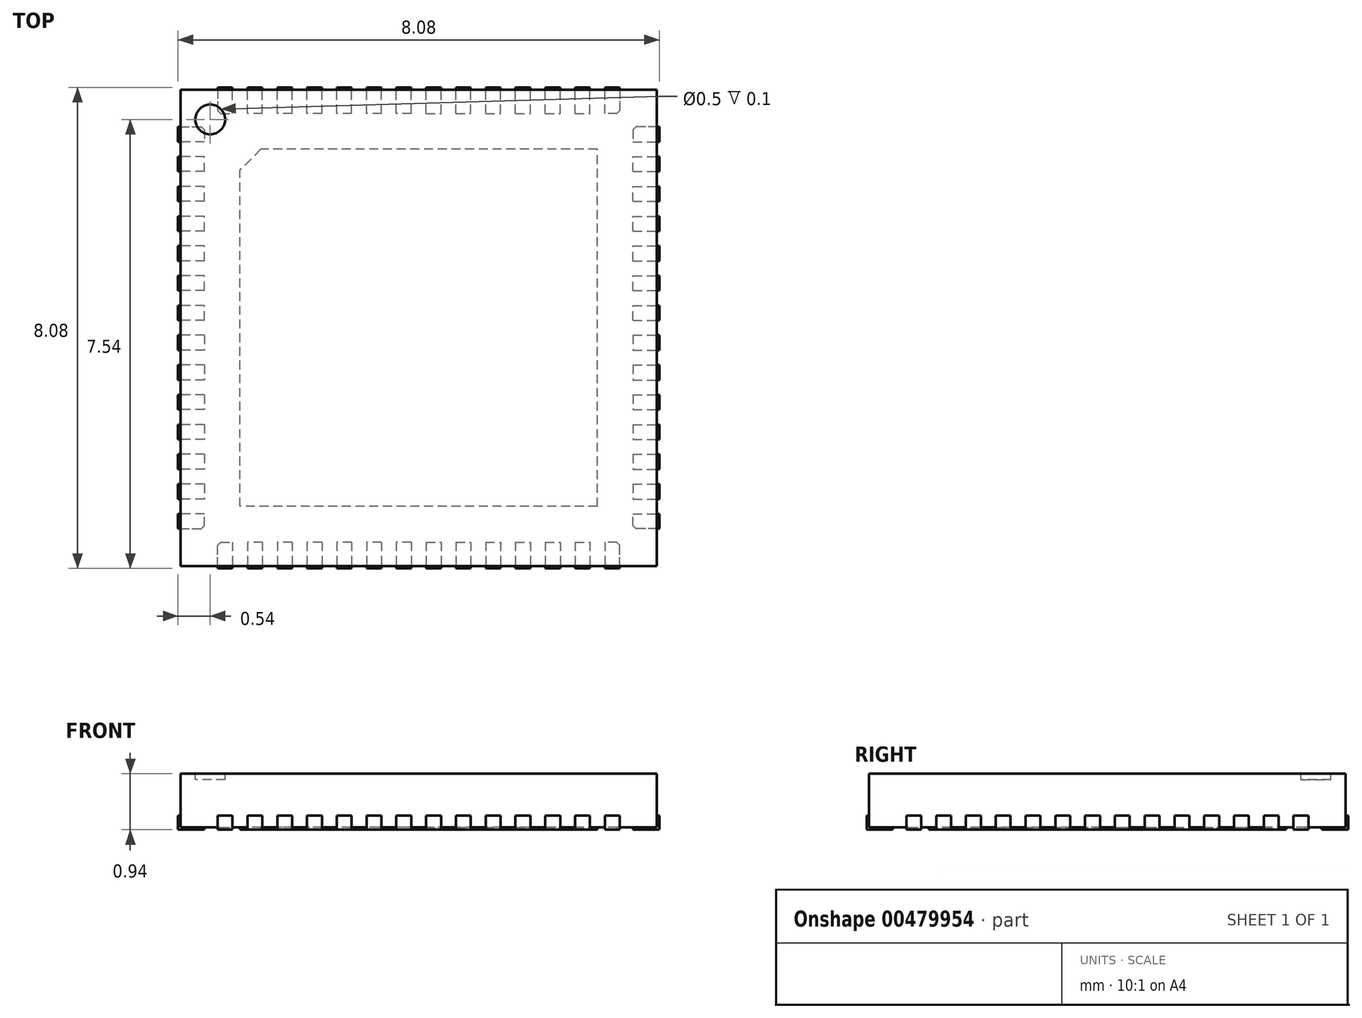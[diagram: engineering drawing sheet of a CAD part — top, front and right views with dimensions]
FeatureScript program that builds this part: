
annotation { "Feature Type Name" : "Feature", "Feature Type Description" : "" }
export const myFeature = defineFeature(function(context is Context, id is Id, definition is map)
    precondition{}
    {
        {
            var Q0;
            Q0=qCreatedBy(makeId("Top.planeOp"),FACE);
            var sketch = newSketch(context, id + "F0", { "sketchPlane" : qUnion([Q0])});
            skLineSegment(sketch, "E0.bottom", {"start": v(4, -4) * mm, "end": v(-4, -4) * mm});
            skLineSegment(sketch, "E0.top", {"start": v(4, 4) * mm, "end": v(-4, 4) * mm});
            skLineSegment(sketch, "E0.left", {"start": v(4, -4) * mm, "end": v(4, 4) * mm});
            skLineSegment(sketch, "E0.right", {"start": v(-4, -4) * mm, "end": v(-4, 4) * mm});
            skPoint(sketch, "E0.middle", {"position": v(0, 0) * mm});
            skSolve(sketch);
        }
        {
            var Q0;
            Q0 = qSketchRegion(id + "F0", true);
            extrude(context, id + "F1", {"entities" : qUnion([Q0]), "depth" : 0.9 * mm});
        }
        {
            var Q0;
            Q0=makeQuery(id+"F1.opExtrude","CAP_FACE",FACE,{"disambiguationData":[OSD([sQuery(id+"F0.wireOp",EDGE,"E0.bottom"),sQuery(id+"F0.wireOp",EDGE,"E0.top"),sQuery(id+"F0.wireOp",EDGE,"E0.left"),sQuery(id+"F0.wireOp",EDGE,"E0.right")])],"isStart":false});
            var sketch = newSketch(context, id + "F2", { "sketchPlane" : qUnion([Q0])});
            skCircle(sketch, "E1", {"center": v(-3.5, 3.5) * mm, "radius": 0.25 * mm});
            skSolve(sketch);
        }
        {
            var Q0;
            Q0 = qSketchRegion(id + "F2", true);
            extrude(context, id + "F3", {"entities" : qUnion([Q0]), "operationType" : NewBodyOperationType.REMOVE, "oppositeDirection" : true, "depth" : 0.1 * mm});
        }
        {
            var Q0;
            Q0=qCreatedBy(makeId("Top.planeOp"),FACE);
            cPlane(context, id + "F4", {"entities" : qUnion([Q0]), "cplaneType" : CPlaneType.OFFSET, "offset" : 0.2 * mm, "width" : 150 * mm, "height" : 150 * mm});
        }
        {
            var Q0;
            Q0=qCreatedBy(id+"F4.planeOp",FACE);
            var sketch = newSketch(context, id + "F5", { "sketchPlane" : qUnion([Q0])});
            skLineSegment(sketch, "E2.bottom", {"start": v(3.6, -2.63) * mm, "end": v(4.04, -2.63) * mm});
            skLineSegment(sketch, "E2.top", {"start": v(3.6, -2.88) * mm, "end": v(4.04, -2.88) * mm});
            skLineSegment(sketch, "E2.left", {"start": v(3.6, -2.63) * mm, "end": v(3.6, -2.88) * mm});
            skLineSegment(sketch, "E2.right", {"start": v(4.04, -2.63) * mm, "end": v(4.04, -2.88) * mm});
            skLineSegment(sketch, "E3.0.1.0", {"start": v(3.6, -2.13) * mm, "end": v(4.04, -2.13) * mm});
            skLineSegment(sketch, "E3.0.1.1", {"start": v(4.04, -2.13) * mm, "end": v(4.04, -2.38) * mm});
            skLineSegment(sketch, "E3.0.1.2", {"start": v(3.6, -2.13) * mm, "end": v(3.6, -2.38) * mm});
            skLineSegment(sketch, "E3.0.1.3", {"start": v(3.6, -2.38) * mm, "end": v(4.04, -2.38) * mm});
            skLineSegment(sketch, "E3.0.2.0", {"start": v(3.6, -1.63) * mm, "end": v(4.04, -1.63) * mm});
            skLineSegment(sketch, "E3.0.2.1", {"start": v(4.04, -1.63) * mm, "end": v(4.04, -1.88) * mm});
            skLineSegment(sketch, "E3.0.2.2", {"start": v(3.6, -1.63) * mm, "end": v(3.6, -1.88) * mm});
            skLineSegment(sketch, "E3.0.2.3", {"start": v(3.6, -1.88) * mm, "end": v(4.04, -1.88) * mm});
            skLineSegment(sketch, "E3.0.3.0", {"start": v(3.6, -1.13) * mm, "end": v(4.04, -1.13) * mm});
            skLineSegment(sketch, "E3.0.3.1", {"start": v(4.04, -1.13) * mm, "end": v(4.04, -1.38) * mm});
            skLineSegment(sketch, "E3.0.3.2", {"start": v(3.6, -1.13) * mm, "end": v(3.6, -1.38) * mm});
            skLineSegment(sketch, "E3.0.3.3", {"start": v(3.6, -1.38) * mm, "end": v(4.04, -1.38) * mm});
            skLineSegment(sketch, "E3.0.4.0", {"start": v(3.6, -0.63) * mm, "end": v(4.04, -0.63) * mm});
            skLineSegment(sketch, "E3.0.4.1", {"start": v(4.04, -0.63) * mm, "end": v(4.04, -0.88) * mm});
            skLineSegment(sketch, "E3.0.4.2", {"start": v(3.6, -0.63) * mm, "end": v(3.6, -0.88) * mm});
            skLineSegment(sketch, "E3.0.4.3", {"start": v(3.6, -0.88) * mm, "end": v(4.04, -0.88) * mm});
            skLineSegment(sketch, "E3.0.5.0", {"start": v(3.6, -0.13) * mm, "end": v(4.04, -0.13) * mm});
            skLineSegment(sketch, "E3.0.5.1", {"start": v(4.04, -0.12) * mm, "end": v(4.04, -0.37) * mm});
            skLineSegment(sketch, "E3.0.5.2", {"start": v(3.6, -0.13) * mm, "end": v(3.6, -0.37) * mm});
            skLineSegment(sketch, "E3.0.5.3", {"start": v(3.6, -0.37) * mm, "end": v(4.04, -0.37) * mm});
            skLineSegment(sketch, "E3.direction1", {"start": v(3.6, -2.88) * mm, "end": v(4.04, -2.88) * mm, "construction": true});
            skLineSegment(sketch, "E3.direction2", {"start": v(3.6, -2.88) * mm, "end": v(3.6, -2.38) * mm, "construction": true});
            skLineSegment(sketch, "E4", {"start": v(3.6, -3.13) * mm, "end": v(4.04, -3.13) * mm});
            skLineSegment(sketch, "E5", {"start": v(4.04, -3.13) * mm, "end": v(4.04, -3.38) * mm});
            skLineSegment(sketch, "E6", {"start": v(4.04, -3.38) * mm, "end": v(3.65, -3.38) * mm});
            skLineSegment(sketch, "E7", {"start": v(3.65, -3.38) * mm, "end": v(3.6, -3.33) * mm});
            skLineSegment(sketch, "E8", {"start": v(3.6, -3.33) * mm, "end": v(3.6, -3.13) * mm});
            skLineSegment(sketch, "E9", {"start": v(41.34, -41.34) * mm, "end": v(-33.82, 33.82) * mm, "construction": true});
            skLineSegment(sketch, "E10", {"start": v(54.18, 0) * mm, "end": v(-46.02, 0) * mm, "construction": true});
            skLineSegment(sketch, "E11.MirrorCS", {"start": v(3.38, -4.04) * mm, "end": v(3.38, -3.65) * mm});
            skLineSegment(sketch, "E12.MirrorCS", {"start": v(3.38, -3.65) * mm, "end": v(3.33, -3.6) * mm});
            skLineSegment(sketch, "E13.MirrorCS", {"start": v(3.13, -4.04) * mm, "end": v(3.38, -4.04) * mm});
            skLineSegment(sketch, "E14.MirrorCS", {"start": v(3.33, -3.6) * mm, "end": v(3.13, -3.6) * mm});
            skLineSegment(sketch, "E15.MirrorCS", {"start": v(3.13, -3.6) * mm, "end": v(3.13, -4.04) * mm});
            skLineSegment(sketch, "E16.MirrorCS", {"start": v(2.88, -3.6) * mm, "end": v(2.38, -3.6) * mm, "construction": true});
            skLineSegment(sketch, "E17.MirrorCS", {"start": v(0.13, -3.6) * mm, "end": v(0.37, -3.6) * mm});
            skLineSegment(sketch, "E18.MirrorCS", {"start": v(0.12, -4.04) * mm, "end": v(0.37, -4.04) * mm});
            skLineSegment(sketch, "E19.MirrorCS", {"start": v(1.63, -3.6) * mm, "end": v(1.88, -3.6) * mm});
            skLineSegment(sketch, "E20.MirrorCS", {"start": v(1.63, -4.04) * mm, "end": v(1.88, -4.04) * mm});
            skLineSegment(sketch, "E21.MirrorCS", {"start": v(2.13, -3.6) * mm, "end": v(2.38, -3.6) * mm});
            skLineSegment(sketch, "E22.MirrorCS", {"start": v(2.13, -4.04) * mm, "end": v(2.38, -4.04) * mm});
            skLineSegment(sketch, "E23.MirrorCS", {"start": v(2.63, -4.04) * mm, "end": v(2.88, -4.04) * mm});
            skLineSegment(sketch, "E24.MirrorCS", {"start": v(2.63, -3.6) * mm, "end": v(2.88, -3.6) * mm});
            skLineSegment(sketch, "E25.MirrorCS", {"start": v(1.13, -3.6) * mm, "end": v(1.38, -3.6) * mm});
            skLineSegment(sketch, "E26.MirrorCS", {"start": v(1.13, -4.04) * mm, "end": v(1.38, -4.04) * mm});
            skLineSegment(sketch, "E27.MirrorCS", {"start": v(1.88, -3.6) * mm, "end": v(1.88, -4.04) * mm});
            skLineSegment(sketch, "E28.MirrorCS", {"start": v(2.88, -3.6) * mm, "end": v(2.88, -4.04) * mm});
            skLineSegment(sketch, "E29.MirrorCS", {"start": v(0.63, -4.04) * mm, "end": v(0.88, -4.04) * mm});
            skLineSegment(sketch, "E30.MirrorCS", {"start": v(0.63, -3.6) * mm, "end": v(0.88, -3.6) * mm});
            skLineSegment(sketch, "E31.MirrorCS", {"start": v(0.88, -3.6) * mm, "end": v(0.88, -4.04) * mm});
            skLineSegment(sketch, "E32.MirrorCS", {"start": v(1.63, -3.6) * mm, "end": v(1.63, -4.04) * mm});
            skLineSegment(sketch, "E33.MirrorCS", {"start": v(2.38, -3.6) * mm, "end": v(2.38, -4.04) * mm});
            skLineSegment(sketch, "E34.MirrorCS", {"start": v(2.13, -3.6) * mm, "end": v(2.13, -4.04) * mm});
            skLineSegment(sketch, "E35.MirrorCS", {"start": v(2.88, -3.6) * mm, "end": v(2.88, -4.04) * mm, "construction": true});
            skLineSegment(sketch, "E36.MirrorCS", {"start": v(0.63, -3.6) * mm, "end": v(0.63, -4.04) * mm});
            skLineSegment(sketch, "E37.MirrorCS", {"start": v(0.38, -3.6) * mm, "end": v(0.38, -4.04) * mm});
            skLineSegment(sketch, "E38.MirrorCS", {"start": v(2.63, -3.6) * mm, "end": v(2.63, -4.04) * mm});
            skLineSegment(sketch, "E39.MirrorCS", {"start": v(1.38, -3.6) * mm, "end": v(1.38, -4.04) * mm});
            skLineSegment(sketch, "E40.MirrorCS", {"start": v(1.13, -3.6) * mm, "end": v(1.13, -4.04) * mm});
            skLineSegment(sketch, "E41.MirrorCS", {"start": v(0.13, -3.6) * mm, "end": v(0.13, -4.04) * mm});
            skLineSegment(sketch, "E42", {"start": v(0, -44.45) * mm, "end": v(0, 45.74) * mm, "construction": true});
            skLineSegment(sketch, "E43.MirrorCS", {"start": v(-3.33, -3.6) * mm, "end": v(-3.13, -3.6) * mm});
            skLineSegment(sketch, "E44.MirrorCS", {"start": v(-3.13, -4.04) * mm, "end": v(-3.38, -4.04) * mm});
            skLineSegment(sketch, "E45.MirrorCS", {"start": v(-3.38, -3.65) * mm, "end": v(-3.33, -3.6) * mm});
            skLineSegment(sketch, "E46.MirrorCS", {"start": v(-3.65, -3.38) * mm, "end": v(-3.6, -3.33) * mm});
            skLineSegment(sketch, "E47.MirrorCS", {"start": v(-4.04, -2.13) * mm, "end": v(-4.04, -2.38) * mm});
            skLineSegment(sketch, "E48.MirrorCS", {"start": v(-3.6, -2.13) * mm, "end": v(-3.6, -2.38) * mm});
            skLineSegment(sketch, "E49.MirrorCS", {"start": v(-4.04, -1.63) * mm, "end": v(-4.04, -1.88) * mm});
            skLineSegment(sketch, "E50.MirrorCS", {"start": v(-3.6, -1.63) * mm, "end": v(-3.6, -1.88) * mm});
            skLineSegment(sketch, "E51.MirrorCS", {"start": v(-0.63, -3.6) * mm, "end": v(-0.88, -3.6) * mm});
            skLineSegment(sketch, "E52.MirrorCS", {"start": v(-0.13, -3.6) * mm, "end": v(-0.37, -3.6) * mm});
            skLineSegment(sketch, "E53.MirrorCS", {"start": v(-3.6, -0.13) * mm, "end": v(-3.6, -0.37) * mm});
            skLineSegment(sketch, "E54.MirrorCS", {"start": v(-1.63, -3.6) * mm, "end": v(-1.88, -3.6) * mm});
            skLineSegment(sketch, "E55.MirrorCS", {"start": v(-0.12, -4.04) * mm, "end": v(-0.37, -4.04) * mm});
            skLineSegment(sketch, "E56.MirrorCS", {"start": v(-2.63, -4.04) * mm, "end": v(-2.88, -4.04) * mm});
            skLineSegment(sketch, "E57.MirrorCS", {"start": v(-3.6, -3.33) * mm, "end": v(-3.6, -3.13) * mm});
            skLineSegment(sketch, "E58.MirrorCS", {"start": v(-4.04, -2.63) * mm, "end": v(-4.04, -2.88) * mm});
            skLineSegment(sketch, "E59.MirrorCS", {"start": v(-3.6, -2.63) * mm, "end": v(-3.6, -2.88) * mm});
            skLineSegment(sketch, "E60.MirrorCS", {"start": v(-2.88, -3.6) * mm, "end": v(-2.38, -3.6) * mm, "construction": true});
            skLineSegment(sketch, "E61.MirrorCS", {"start": v(-3.6, -1.13) * mm, "end": v(-3.6, -1.38) * mm});
            skLineSegment(sketch, "E62.MirrorCS", {"start": v(-2.13, -4.04) * mm, "end": v(-2.38, -4.04) * mm});
            skLineSegment(sketch, "E63.MirrorCS", {"start": v(-1.13, -3.6) * mm, "end": v(-1.38, -3.6) * mm});
            skLineSegment(sketch, "E64.MirrorCS", {"start": v(-4.04, -0.12) * mm, "end": v(-4.04, -0.37) * mm});
            skLineSegment(sketch, "E65.MirrorCS", {"start": v(-0.63, -4.04) * mm, "end": v(-0.88, -4.04) * mm});
            skLineSegment(sketch, "E66.MirrorCS", {"start": v(-4.04, -3.13) * mm, "end": v(-4.04, -3.38) * mm});
            skLineSegment(sketch, "E67.MirrorCS", {"start": v(-1.63, -4.04) * mm, "end": v(-1.88, -4.04) * mm});
            skLineSegment(sketch, "E68.MirrorCS", {"start": v(-1.13, -4.04) * mm, "end": v(-1.38, -4.04) * mm});
            skLineSegment(sketch, "E69.MirrorCS", {"start": v(-4.04, -0.63) * mm, "end": v(-4.04, -0.88) * mm});
            skLineSegment(sketch, "E70.MirrorCS", {"start": v(-3.6, -2.88) * mm, "end": v(-3.6, -2.38) * mm, "construction": true});
            skLineSegment(sketch, "E71.MirrorCS", {"start": v(-2.13, -3.6) * mm, "end": v(-2.38, -3.6) * mm});
            skLineSegment(sketch, "E72.MirrorCS", {"start": v(-3.6, -0.63) * mm, "end": v(-3.6, -0.88) * mm});
            skLineSegment(sketch, "E73.MirrorCS", {"start": v(-2.63, -3.6) * mm, "end": v(-2.88, -3.6) * mm});
            skLineSegment(sketch, "E74.MirrorCS", {"start": v(-3.13, -3.6) * mm, "end": v(-3.13, -4.04) * mm});
            skLineSegment(sketch, "E75.MirrorCS", {"start": v(-4.04, -1.13) * mm, "end": v(-4.04, -1.38) * mm});
            skLineSegment(sketch, "E76.MirrorCS", {"start": v(-3.38, -4.04) * mm, "end": v(-3.38, -3.65) * mm});
            skLineSegment(sketch, "E77.MirrorCS", {"start": v(-4.04, -3.38) * mm, "end": v(-3.65, -3.38) * mm});
            skLineSegment(sketch, "E78.MirrorCS", {"start": v(-3.6, -1.88) * mm, "end": v(-4.04, -1.88) * mm});
            skLineSegment(sketch, "E79.MirrorCS", {"start": v(-3.6, -2.88) * mm, "end": v(-4.04, -2.88) * mm});
            skLineSegment(sketch, "E80.MirrorCS", {"start": v(-2.88, -3.6) * mm, "end": v(-2.88, -4.04) * mm});
            skLineSegment(sketch, "E81.MirrorCS", {"start": v(-3.6, -2.13) * mm, "end": v(-4.04, -2.13) * mm});
            skLineSegment(sketch, "E82.MirrorCS", {"start": v(-0.63, -3.6) * mm, "end": v(-0.63, -4.04) * mm});
            skLineSegment(sketch, "E83.MirrorCS", {"start": v(-3.6, -2.38) * mm, "end": v(-4.04, -2.38) * mm});
            skLineSegment(sketch, "E84.MirrorCS", {"start": v(-3.6, -1.63) * mm, "end": v(-4.04, -1.63) * mm});
            skLineSegment(sketch, "E85.MirrorCS", {"start": v(-41.34, -41.34) * mm, "end": v(33.82, 33.82) * mm, "construction": true});
            skLineSegment(sketch, "E86.MirrorCS", {"start": v(-3.6, -1.13) * mm, "end": v(-4.04, -1.13) * mm});
            skLineSegment(sketch, "E87.MirrorCS", {"start": v(-54.18, 0) * mm, "end": v(46.02, 0) * mm, "construction": true});
            skLineSegment(sketch, "E88.MirrorCS", {"start": v(-3.6, -0.63) * mm, "end": v(-4.04, -0.63) * mm});
            skLineSegment(sketch, "E89.MirrorCS", {"start": v(-3.6, -0.12) * mm, "end": v(-4.04, -0.12) * mm});
            skLineSegment(sketch, "E90.MirrorCS", {"start": v(-3.6, -2.63) * mm, "end": v(-4.04, -2.63) * mm});
            skLineSegment(sketch, "E91.MirrorCS", {"start": v(-3.6, -1.38) * mm, "end": v(-4.04, -1.38) * mm});
            skLineSegment(sketch, "E92.MirrorCS", {"start": v(-1.38, -3.6) * mm, "end": v(-1.38, -4.04) * mm});
            skLineSegment(sketch, "E93.MirrorCS", {"start": v(-3.6, -0.37) * mm, "end": v(-4.04, -0.37) * mm});
            skLineSegment(sketch, "E94.MirrorCS", {"start": v(-1.13, -3.6) * mm, "end": v(-1.13, -4.04) * mm});
            skLineSegment(sketch, "E95.MirrorCS", {"start": v(-3.6, -2.88) * mm, "end": v(-4.04, -2.88) * mm, "construction": true});
            skLineSegment(sketch, "E96.MirrorCS", {"start": v(-0.38, -3.6) * mm, "end": v(-0.38, -4.04) * mm});
            skLineSegment(sketch, "E97.MirrorCS", {"start": v(-0.88, -3.6) * mm, "end": v(-0.88, -4.04) * mm});
            skLineSegment(sketch, "E98.MirrorCS", {"start": v(-0.13, -3.6) * mm, "end": v(-0.13, -4.04) * mm});
            skLineSegment(sketch, "E99.MirrorCS", {"start": v(-1.88, -3.6) * mm, "end": v(-1.88, -4.04) * mm});
            skLineSegment(sketch, "E100.MirrorCS", {"start": v(-2.13, -3.6) * mm, "end": v(-2.13, -4.04) * mm});
            skLineSegment(sketch, "E101.MirrorCS", {"start": v(-2.88, -3.6) * mm, "end": v(-2.88, -4.04) * mm, "construction": true});
            skLineSegment(sketch, "E102.MirrorCS", {"start": v(-3.6, -0.88) * mm, "end": v(-4.04, -0.88) * mm});
            skLineSegment(sketch, "E103.MirrorCS", {"start": v(-1.63, -3.6) * mm, "end": v(-1.63, -4.04) * mm});
            skLineSegment(sketch, "E104.MirrorCS", {"start": v(-2.63, -3.6) * mm, "end": v(-2.63, -4.04) * mm});
            skLineSegment(sketch, "E105.MirrorCS", {"start": v(-2.38, -3.6) * mm, "end": v(-2.38, -4.04) * mm});
            skLineSegment(sketch, "E106.MirrorCS", {"start": v(-3.6, -3.13) * mm, "end": v(-4.04, -3.13) * mm});
            skLineSegment(sketch, "E107.MirrorCS", {"start": v(3.33, 3.6) * mm, "end": v(3.13, 3.6) * mm});
            skLineSegment(sketch, "E108.MirrorCS", {"start": v(3.38, 3.65) * mm, "end": v(3.33, 3.6) * mm});
            skLineSegment(sketch, "E109.MirrorCS", {"start": v(-3.13, 4.04) * mm, "end": v(-3.38, 4.04) * mm});
            skLineSegment(sketch, "E110.MirrorCS", {"start": v(-3.38, 3.65) * mm, "end": v(-3.33, 3.6) * mm});
            skLineSegment(sketch, "E111.MirrorCS", {"start": v(3.13, 4.04) * mm, "end": v(3.38, 4.04) * mm});
            skLineSegment(sketch, "E112.MirrorCS", {"start": v(-3.33, 3.6) * mm, "end": v(-3.13, 3.6) * mm});
            skLineSegment(sketch, "E113.MirrorCS", {"start": v(3.65, 3.38) * mm, "end": v(3.6, 3.33) * mm});
            skLineSegment(sketch, "E114.MirrorCS", {"start": v(-3.6, 0.12) * mm, "end": v(-3.6, 0.37) * mm});
            skLineSegment(sketch, "E115.MirrorCS", {"start": v(4.04, 3.13) * mm, "end": v(4.04, 3.38) * mm});
            skLineSegment(sketch, "E116.MirrorCS", {"start": v(2.88, 3.6) * mm, "end": v(2.38, 3.6) * mm, "construction": true});
            skLineSegment(sketch, "E117.MirrorCS", {"start": v(0.63, 4.04) * mm, "end": v(0.88, 4.04) * mm});
            skLineSegment(sketch, "E118.MirrorCS", {"start": v(-4.04, 0.62) * mm, "end": v(-4.04, 0.87) * mm});
            skLineSegment(sketch, "E119.MirrorCS", {"start": v(-4.04, 2.13) * mm, "end": v(-4.04, 2.38) * mm});
            skLineSegment(sketch, "E120.MirrorCS", {"start": v(-4.04, 1.13) * mm, "end": v(-4.04, 1.38) * mm});
            skLineSegment(sketch, "E121.MirrorCS", {"start": v(1.63, 4.04) * mm, "end": v(1.88, 4.04) * mm});
            skLineSegment(sketch, "E122.MirrorCS", {"start": v(-0.13, 3.6) * mm, "end": v(-0.37, 3.6) * mm});
            skLineSegment(sketch, "E123.MirrorCS", {"start": v(-1.13, 4.04) * mm, "end": v(-1.38, 4.04) * mm});
            skLineSegment(sketch, "E124.MirrorCS", {"start": v(-3.6, 2.63) * mm, "end": v(-3.6, 2.88) * mm});
            skLineSegment(sketch, "E125.MirrorCS", {"start": v(-0.63, 3.6) * mm, "end": v(-0.88, 3.6) * mm});
            skLineSegment(sketch, "E126.MirrorCS", {"start": v(-1.63, 4.04) * mm, "end": v(-1.88, 4.04) * mm});
            skLineSegment(sketch, "E127.MirrorCS", {"start": v(3.6, 2.88) * mm, "end": v(3.6, 2.38) * mm, "construction": true});
            skLineSegment(sketch, "E128.MirrorCS", {"start": v(-3.6, 1.63) * mm, "end": v(-3.6, 1.88) * mm});
            skLineSegment(sketch, "E129.MirrorCS", {"start": v(1.13, 4.04) * mm, "end": v(1.38, 4.04) * mm});
            skLineSegment(sketch, "E130.MirrorCS", {"start": v(-3.65, 3.38) * mm, "end": v(-3.6, 3.33) * mm});
            skLineSegment(sketch, "E131.MirrorCS", {"start": v(-1.13, 3.6) * mm, "end": v(-1.38, 3.6) * mm});
            skLineSegment(sketch, "E132.MirrorCS", {"start": v(-0.63, 4.04) * mm, "end": v(-0.88, 4.04) * mm});
            skLineSegment(sketch, "E133.MirrorCS", {"start": v(2.13, 3.6) * mm, "end": v(2.38, 3.6) * mm});
            skLineSegment(sketch, "E134.MirrorCS", {"start": v(-4.04, 3.13) * mm, "end": v(-4.04, 3.38) * mm});
            skLineSegment(sketch, "E135.MirrorCS", {"start": v(-2.63, 3.6) * mm, "end": v(-2.88, 3.6) * mm});
            skLineSegment(sketch, "E136.MirrorCS", {"start": v(-3.6, 0.62) * mm, "end": v(-3.6, 0.87) * mm});
            skLineSegment(sketch, "E137.MirrorCS", {"start": v(-2.88, 3.6) * mm, "end": v(-2.38, 3.6) * mm, "construction": true});
            skLineSegment(sketch, "E138.MirrorCS", {"start": v(-2.63, 4.04) * mm, "end": v(-2.88, 4.04) * mm});
            skLineSegment(sketch, "E139.MirrorCS", {"start": v(3.6, 3.33) * mm, "end": v(3.6, 3.13) * mm});
            skLineSegment(sketch, "E140.MirrorCS", {"start": v(-1.63, 3.6) * mm, "end": v(-1.88, 3.6) * mm});
            skLineSegment(sketch, "E141.MirrorCS", {"start": v(-3.6, 2.88) * mm, "end": v(-3.6, 2.38) * mm, "construction": true});
            skLineSegment(sketch, "E142.MirrorCS", {"start": v(0.13, 3.6) * mm, "end": v(0.37, 3.6) * mm});
            skLineSegment(sketch, "E143.MirrorCS", {"start": v(-3.13, 3.6) * mm, "end": v(-3.13, 4.04) * mm});
            skLineSegment(sketch, "E144.MirrorCS", {"start": v(3.6, 0.62) * mm, "end": v(3.6, 0.87) * mm});
            skLineSegment(sketch, "E145.MirrorCS", {"start": v(3.38, 4.04) * mm, "end": v(3.38, 3.65) * mm});
            skLineSegment(sketch, "E146.MirrorCS", {"start": v(1.63, 3.6) * mm, "end": v(1.88, 3.6) * mm});
            skLineSegment(sketch, "E147.MirrorCS", {"start": v(-3.6, 3.33) * mm, "end": v(-3.6, 3.13) * mm});
            skLineSegment(sketch, "E148.MirrorCS", {"start": v(-0.12, 4.04) * mm, "end": v(-0.37, 4.04) * mm});
            skLineSegment(sketch, "E149.MirrorCS", {"start": v(0.12, 4.04) * mm, "end": v(0.37, 4.04) * mm});
            skLineSegment(sketch, "E150.MirrorCS", {"start": v(-4.04, 2.63) * mm, "end": v(-4.04, 2.88) * mm});
            skLineSegment(sketch, "E151.MirrorCS", {"start": v(-2.13, 3.6) * mm, "end": v(-2.38, 3.6) * mm});
            skLineSegment(sketch, "E152.MirrorCS", {"start": v(2.13, 4.04) * mm, "end": v(2.38, 4.04) * mm});
            skLineSegment(sketch, "E153.MirrorCS", {"start": v(4.04, 0.12) * mm, "end": v(4.04, 0.37) * mm});
            skLineSegment(sketch, "E154.MirrorCS", {"start": v(-4.04, 0.12) * mm, "end": v(-4.04, 0.37) * mm});
            skLineSegment(sketch, "E155.MirrorCS", {"start": v(-3.6, 2.13) * mm, "end": v(-3.6, 2.38) * mm});
            skLineSegment(sketch, "E156.MirrorCS", {"start": v(0.63, 3.6) * mm, "end": v(0.88, 3.6) * mm});
            skLineSegment(sketch, "E157.MirrorCS", {"start": v(-2.13, 4.04) * mm, "end": v(-2.38, 4.04) * mm});
            skLineSegment(sketch, "E158.MirrorCS", {"start": v(3.6, 0.12) * mm, "end": v(3.6, 0.37) * mm});
            skLineSegment(sketch, "E159.MirrorCS", {"start": v(-3.6, 1.13) * mm, "end": v(-3.6, 1.38) * mm});
            skLineSegment(sketch, "E160.MirrorCS", {"start": v(2.63, 3.6) * mm, "end": v(2.88, 3.6) * mm});
            skLineSegment(sketch, "E161.MirrorCS", {"start": v(3.13, 3.6) * mm, "end": v(3.13, 4.04) * mm});
            skLineSegment(sketch, "E162.MirrorCS", {"start": v(4.04, 1.63) * mm, "end": v(4.04, 1.88) * mm});
            skLineSegment(sketch, "E163.MirrorCS", {"start": v(3.6, 2.13) * mm, "end": v(3.6, 2.38) * mm});
            skLineSegment(sketch, "E164.MirrorCS", {"start": v(4.04, 2.13) * mm, "end": v(4.04, 2.38) * mm});
            skLineSegment(sketch, "E165.MirrorCS", {"start": v(3.6, 1.63) * mm, "end": v(3.6, 1.88) * mm});
            skLineSegment(sketch, "E166.MirrorCS", {"start": v(1.13, 3.6) * mm, "end": v(1.38, 3.6) * mm});
            skLineSegment(sketch, "E167.MirrorCS", {"start": v(2.63, 4.04) * mm, "end": v(2.88, 4.04) * mm});
            skLineSegment(sketch, "E168.MirrorCS", {"start": v(3.6, 1.13) * mm, "end": v(3.6, 1.38) * mm});
            skLineSegment(sketch, "E169.MirrorCS", {"start": v(-3.38, 4.04) * mm, "end": v(-3.38, 3.65) * mm});
            skLineSegment(sketch, "E170.MirrorCS", {"start": v(4.04, 1.13) * mm, "end": v(4.04, 1.38) * mm});
            skLineSegment(sketch, "E171.MirrorCS", {"start": v(-4.04, 1.63) * mm, "end": v(-4.04, 1.88) * mm});
            skLineSegment(sketch, "E172.MirrorCS", {"start": v(4.04, 2.63) * mm, "end": v(4.04, 2.88) * mm});
            skLineSegment(sketch, "E173.MirrorCS", {"start": v(4.04, 0.62) * mm, "end": v(4.04, 0.87) * mm});
            skLineSegment(sketch, "E174.MirrorCS", {"start": v(3.6, 2.63) * mm, "end": v(3.6, 2.88) * mm});
            skLineSegment(sketch, "E175.MirrorCS", {"start": v(-2.88, 3.6) * mm, "end": v(-2.88, 4.04) * mm});
            skLineSegment(sketch, "E176.MirrorCS", {"start": v(3.6, 1.88) * mm, "end": v(4.04, 1.88) * mm});
            skLineSegment(sketch, "E177.MirrorCS", {"start": v(4.04, 3.38) * mm, "end": v(3.65, 3.38) * mm});
            skLineSegment(sketch, "E178.MirrorCS", {"start": v(2.88, 3.6) * mm, "end": v(2.88, 4.04) * mm});
            skLineSegment(sketch, "E179.MirrorCS", {"start": v(-3.6, 2.88) * mm, "end": v(-4.04, 2.88) * mm});
            skLineSegment(sketch, "E180.MirrorCS", {"start": v(3.6, 2.88) * mm, "end": v(4.04, 2.88) * mm});
            skLineSegment(sketch, "E181.MirrorCS", {"start": v(-3.6, 2.38) * mm, "end": v(-4.04, 2.38) * mm});
            skLineSegment(sketch, "E182.MirrorCS", {"start": v(-0.88, 3.6) * mm, "end": v(-0.88, 4.04) * mm});
            skLineSegment(sketch, "E183.MirrorCS", {"start": v(-1.63, 3.6) * mm, "end": v(-1.63, 4.04) * mm});
            skLineSegment(sketch, "E184.MirrorCS", {"start": v(2.38, 3.6) * mm, "end": v(2.38, 4.04) * mm});
            skLineSegment(sketch, "E185.MirrorCS", {"start": v(-0.63, 3.6) * mm, "end": v(-0.63, 4.04) * mm});
            skLineSegment(sketch, "E186.MirrorCS", {"start": v(-0.38, 3.6) * mm, "end": v(-0.38, 4.04) * mm});
            skLineSegment(sketch, "E187.MirrorCS", {"start": v(-3.6, 2.13) * mm, "end": v(-4.04, 2.13) * mm});
            skLineSegment(sketch, "E188.MirrorCS", {"start": v(1.13, 3.6) * mm, "end": v(1.13, 4.04) * mm});
            skLineSegment(sketch, "E189.MirrorCS", {"start": v(-4.04, 3.38) * mm, "end": v(-3.65, 3.38) * mm});
            skLineSegment(sketch, "E190.MirrorCS", {"start": v(-3.6, 3.13) * mm, "end": v(-4.04, 3.13) * mm});
            skLineSegment(sketch, "E191.MirrorCS", {"start": v(3.6, 0.12) * mm, "end": v(4.04, 0.12) * mm});
            skLineSegment(sketch, "E192.MirrorCS", {"start": v(-1.13, 3.6) * mm, "end": v(-1.13, 4.04) * mm});
            skLineSegment(sketch, "E193.MirrorCS", {"start": v(3.6, 0.37) * mm, "end": v(4.04, 0.37) * mm});
            skLineSegment(sketch, "E194.MirrorCS", {"start": v(-3.6, 2.88) * mm, "end": v(-4.04, 2.88) * mm, "construction": true});
            skLineSegment(sketch, "E195.MirrorCS", {"start": v(0.38, 3.6) * mm, "end": v(0.38, 4.04) * mm});
            skLineSegment(sketch, "E196.MirrorCS", {"start": v(-3.6, 1.13) * mm, "end": v(-4.04, 1.13) * mm});
            skLineSegment(sketch, "E197.MirrorCS", {"start": v(-2.13, 3.6) * mm, "end": v(-2.13, 4.04) * mm});
            skLineSegment(sketch, "E198.MirrorCS", {"start": v(2.13, 3.6) * mm, "end": v(2.13, 4.04) * mm});
            skLineSegment(sketch, "E199.MirrorCS", {"start": v(0.88, 3.6) * mm, "end": v(0.88, 4.04) * mm});
            skLineSegment(sketch, "E200.MirrorCS", {"start": v(3.6, 1.13) * mm, "end": v(4.04, 1.13) * mm});
            skLineSegment(sketch, "E201.MirrorCS", {"start": v(-3.6, 1.63) * mm, "end": v(-4.04, 1.63) * mm});
            skLineSegment(sketch, "E202.MirrorCS", {"start": v(-0.13, 3.6) * mm, "end": v(-0.13, 4.04) * mm});
            skLineSegment(sketch, "E203.MirrorCS", {"start": v(-2.88, 3.6) * mm, "end": v(-2.88, 4.04) * mm, "construction": true});
            skLineSegment(sketch, "E204.MirrorCS", {"start": v(-3.6, 1.88) * mm, "end": v(-4.04, 1.88) * mm});
            skLineSegment(sketch, "E205.MirrorCS", {"start": v(-1.38, 3.6) * mm, "end": v(-1.38, 4.04) * mm});
            skLineSegment(sketch, "E206.MirrorCS", {"start": v(3.6, 3.13) * mm, "end": v(4.04, 3.13) * mm});
            skLineSegment(sketch, "E207.MirrorCS", {"start": v(-3.6, 0.62) * mm, "end": v(-4.04, 0.62) * mm});
            skLineSegment(sketch, "E208.MirrorCS", {"start": v(-3.6, 0.87) * mm, "end": v(-4.04, 0.87) * mm});
            skLineSegment(sketch, "E209.MirrorCS", {"start": v(1.63, 3.6) * mm, "end": v(1.63, 4.04) * mm});
            skLineSegment(sketch, "E210.MirrorCS", {"start": v(3.6, 2.88) * mm, "end": v(4.04, 2.88) * mm, "construction": true});
            skLineSegment(sketch, "E211.MirrorCS", {"start": v(-1.88, 3.6) * mm, "end": v(-1.88, 4.04) * mm});
            skLineSegment(sketch, "E212.MirrorCS", {"start": v(-3.6, 2.63) * mm, "end": v(-4.04, 2.63) * mm});
            skLineSegment(sketch, "E213.MirrorCS", {"start": v(3.6, 0.62) * mm, "end": v(4.04, 0.62) * mm});
            skLineSegment(sketch, "E214.MirrorCS", {"start": v(-2.38, 3.6) * mm, "end": v(-2.38, 4.04) * mm});
            skLineSegment(sketch, "E215.MirrorCS", {"start": v(2.88, 3.6) * mm, "end": v(2.88, 4.04) * mm, "construction": true});
            skLineSegment(sketch, "E216.MirrorCS", {"start": v(-3.6, 1.38) * mm, "end": v(-4.04, 1.38) * mm});
            skLineSegment(sketch, "E217.MirrorCS", {"start": v(3.6, 0.87) * mm, "end": v(4.04, 0.87) * mm});
            skLineSegment(sketch, "E218.MirrorCS", {"start": v(2.63, 3.6) * mm, "end": v(2.63, 4.04) * mm});
            skLineSegment(sketch, "E219.MirrorCS", {"start": v(3.6, 1.38) * mm, "end": v(4.04, 1.38) * mm});
            skLineSegment(sketch, "E220.MirrorCS", {"start": v(0.63, 3.6) * mm, "end": v(0.63, 4.04) * mm});
            skLineSegment(sketch, "E221.MirrorCS", {"start": v(3.6, 2.63) * mm, "end": v(4.04, 2.63) * mm});
            skLineSegment(sketch, "E222.MirrorCS", {"start": v(3.6, 1.63) * mm, "end": v(4.04, 1.63) * mm});
            skLineSegment(sketch, "E223.MirrorCS", {"start": v(3.6, 2.38) * mm, "end": v(4.04, 2.38) * mm});
            skLineSegment(sketch, "E224.MirrorCS", {"start": v(1.38, 3.6) * mm, "end": v(1.38, 4.04) * mm});
            skLineSegment(sketch, "E225.MirrorCS", {"start": v(-3.6, 0.12) * mm, "end": v(-4.04, 0.12) * mm});
            skLineSegment(sketch, "E226.MirrorCS", {"start": v(3.6, 2.13) * mm, "end": v(4.04, 2.13) * mm});
            skLineSegment(sketch, "E227.MirrorCS", {"start": v(-3.6, 0.37) * mm, "end": v(-4.04, 0.37) * mm});
            skLineSegment(sketch, "E228.MirrorCS", {"start": v(1.88, 3.6) * mm, "end": v(1.88, 4.04) * mm});
            skLineSegment(sketch, "E229.MirrorCS", {"start": v(-2.63, 3.6) * mm, "end": v(-2.63, 4.04) * mm});
            skLineSegment(sketch, "E230.MirrorCS", {"start": v(0.13, 3.6) * mm, "end": v(0.13, 4.04) * mm});
            skPoint(sketch, "E231.middle", {"position": v(0, 0) * mm});
            skSolve(sketch);
        }
        {
            var Q0;
            Q0=qCreatedBy(id+"F4.planeOp",FACE);
            var sketch = newSketch(context, id + "F6", { "sketchPlane" : qUnion([Q0])});
            skLineSegment(sketch, "E232.bottom", {"start": v(3.6, 3.6) * mm, "end": v(-3.6, 3.6) * mm});
            skLineSegment(sketch, "E232.top", {"start": v(3.6, -3.6) * mm, "end": v(-3.6, -3.6) * mm});
            skLineSegment(sketch, "E232.left", {"start": v(3.6, 3.6) * mm, "end": v(3.6, -3.6) * mm});
            skLineSegment(sketch, "E232.right", {"start": v(-3.6, 3.6) * mm, "end": v(-3.6, -3.6) * mm});
            skPoint(sketch, "E232.middle", {"position": v(0, 0) * mm});
            skSolve(sketch);
        }
        {
            var Q0;
            Q0 = qSketchRegion(id + "F6", true);
            extrude(context, id + "F7", {"entities" : qUnion([Q0]), "oppositeDirection" : true, "depth" : 0.1 * mm});
        }
        {
            var Q0;
            Q0 = qSketchRegion(id + "F5", true);
            extrude(context, id + "F8", {"entities" : qUnion([Q0]), "operationType" : NewBodyOperationType.ADD, "oppositeDirection" : true, "depth" : 0.24 * mm});
        }
        {
            var Q0;
            Q0=qCreatedBy(makeId("Top.planeOp"),FACE);
            var sketch = newSketch(context, id + "F9", { "sketchPlane" : qUnion([Q0])});
            skLineSegment(sketch, "E233.bottom", {"start": v(3, -3) * mm, "end": v(-3, -3) * mm});
            skLineSegment(sketch, "E233.top", {"start": v(3, 3) * mm, "end": v(-3, 3) * mm});
            skLineSegment(sketch, "E233.left", {"start": v(3, -3) * mm, "end": v(3, 3) * mm});
            skLineSegment(sketch, "E233.right", {"start": v(-3, -3) * mm, "end": v(-3, 3) * mm});
            skPoint(sketch, "E233.middle", {"position": v(0, 0) * mm});
            skLineSegment(sketch, "E234", {"start": v(-2.65, 3) * mm, "end": v(-3, 2.65) * mm});
            skSolve(sketch);
        }
        {
            var Q0;
            {var subQ1=sQuery(id+"F9.wireOp",EDGE,"E233.bottom");Q0=makeQuery(id+"F9.imprint","IMPRINT",FACE,{"disambiguationData":[TD([[makeQuery(id+"F9.imprint","IMPRINT",EDGE,{"derivedFrom":subQ1}),-1.0]])]});}
            extrude(context, id + "F10", {"entities" : qUnion([Q0]), "oppositeDirection" : true, "depth" : 0.04 * mm});
        }
    });
